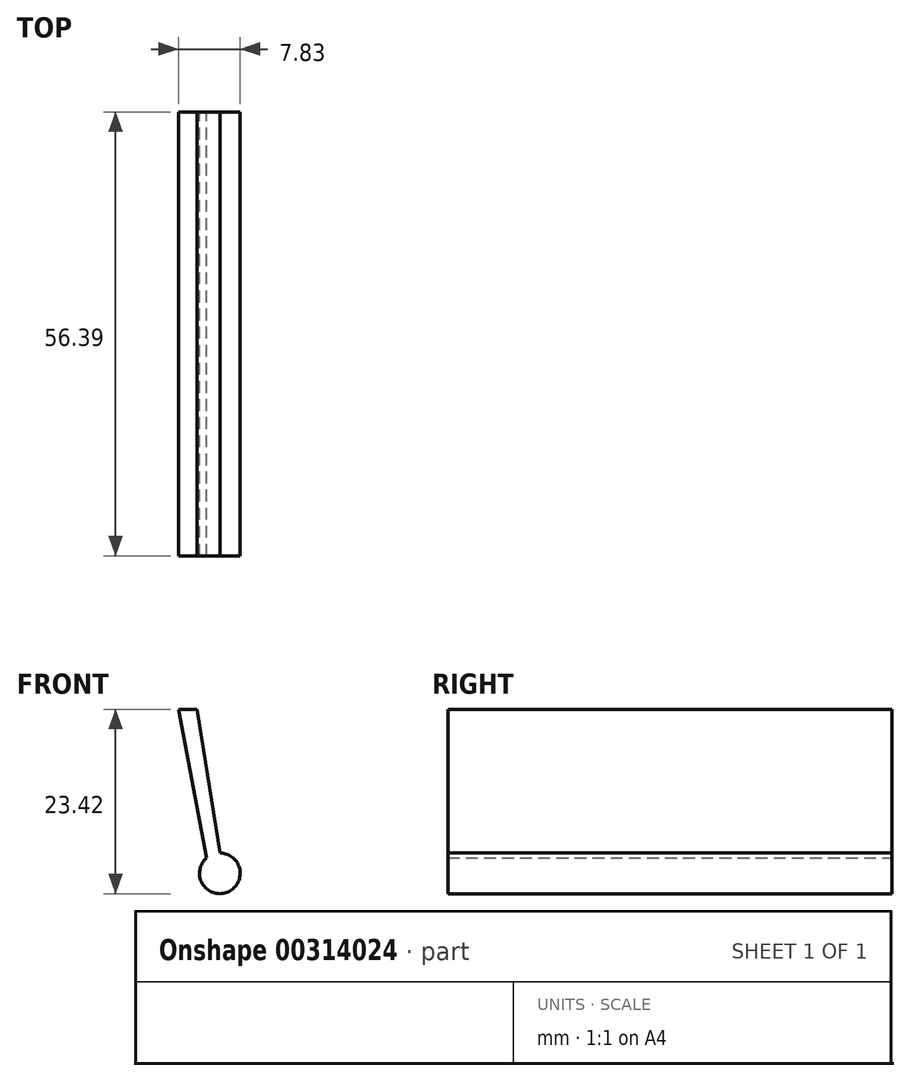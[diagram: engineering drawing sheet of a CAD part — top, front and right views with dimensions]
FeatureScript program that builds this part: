
annotation { "Feature Type Name" : "Feature", "Feature Type Description" : "" }
export const myFeature = defineFeature(function(context is Context, id is Id, definition is map)
    precondition{}
    {
        {
            var Q0;
            Q0=qCreatedBy(makeId("Front.planeOp"),FACE);
            var sketch = newSketch(context, id + "F0", { "sketchPlane" : qUnion([Q0])});
            skCircle(sketch, "E0", {"center": v(0, 0) * mm, "radius": 2.58 * mm});
            skLineSegment(sketch, "E1", {"start": v(0, 2.58) * mm, "end": v(-2.91, 20.84) * mm});
            skLineSegment(sketch, "E2", {"start": v(-2.91, 20.84) * mm, "end": v(-5.25, 20.84) * mm});
            skLineSegment(sketch, "E3", {"start": v(-5.25, 20.84) * mm, "end": v(-1.66, 1.97) * mm});
            skSolve(sketch);
        }
        {
            var Q0;
            Q0 = qSketchRegion(id + "F0", true);
            extrude(context, id + "F1", {"entities" : qUnion([Q0]), "depth" : 56.4 * mm});
        }
    });
